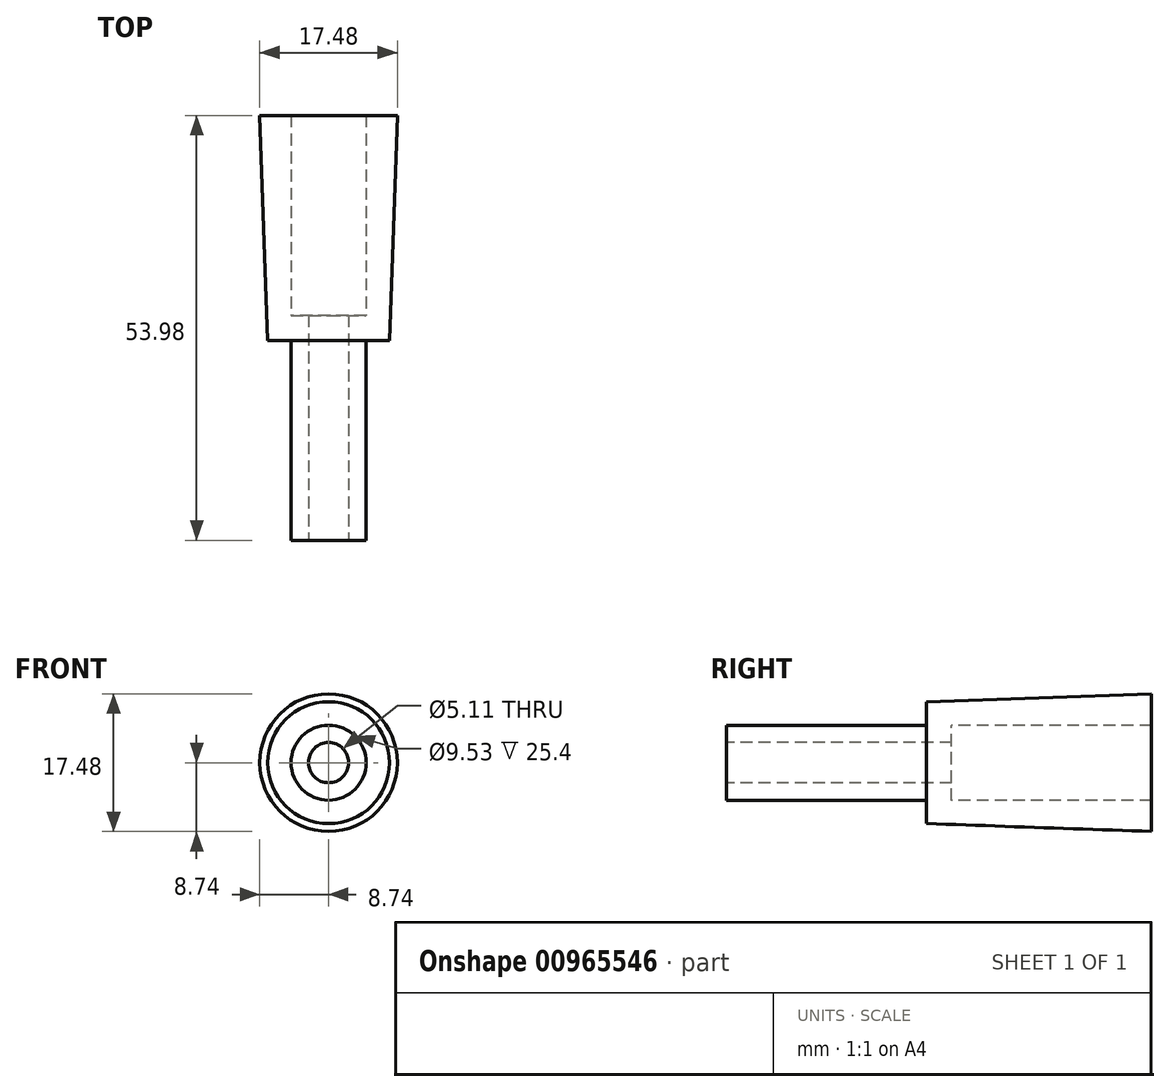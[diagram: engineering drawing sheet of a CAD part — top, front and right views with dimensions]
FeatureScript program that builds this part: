
annotation { "Feature Type Name" : "Feature", "Feature Type Description" : "" }
export const myFeature = defineFeature(function(context is Context, id is Id, definition is map)
    precondition{}
    {
        {
            var Q0;
            Q0=qCreatedBy(makeId("Right.planeOp"),FACE);
            var sketch = newSketch(context, id + "F0", { "sketchPlane" : qUnion([Q0])});
            skLineSegment(sketch, "E0", {"start": v(5.87, 0) * mm, "end": v(165.81, 0) * mm, "construction": true});
            skLineSegment(sketch, "E1", {"start": v(-25.4, 4.76) * mm, "end": v(0, 4.76) * mm});
            skLineSegment(sketch, "E2", {"start": v(0, 4.76) * mm, "end": v(0, 7.74) * mm});
            skLineSegment(sketch, "E3", {"start": v(0, 7.74) * mm, "end": v(28.57, 8.74) * mm});
            skLineSegment(sketch, "E4", {"start": v(28.58, 8.74) * mm, "end": v(28.58, 4.76) * mm});
            skLineSegment(sketch, "E5", {"start": v(28.58, 4.76) * mm, "end": v(3.18, 4.76) * mm});
            skLineSegment(sketch, "E6", {"start": v(3.18, 4.76) * mm, "end": v(3.18, 2.55) * mm});
            skLineSegment(sketch, "E7", {"start": v(3.18, 2.55) * mm, "end": v(-25.4, 2.55) * mm});
            skLineSegment(sketch, "E8", {"start": v(-25.4, 2.55) * mm, "end": v(-25.4, 4.76) * mm});
            skSolve(sketch);
        }
        {
            var Q0;
            Q0=qSketchRegion(id+"F0",true);
            var Q1;
            Q1=sQuery(id+"F0.wireOp",EDGE,"E0");
            revolve(context, id + "F1", {"surfaceOperationType" : NewSurfaceOperationType.NEW, "entities" : qUnion([Q0]), "axis" : qUnion([Q1]), "revolveType" : RevolveType.FULL});
        }
    });
